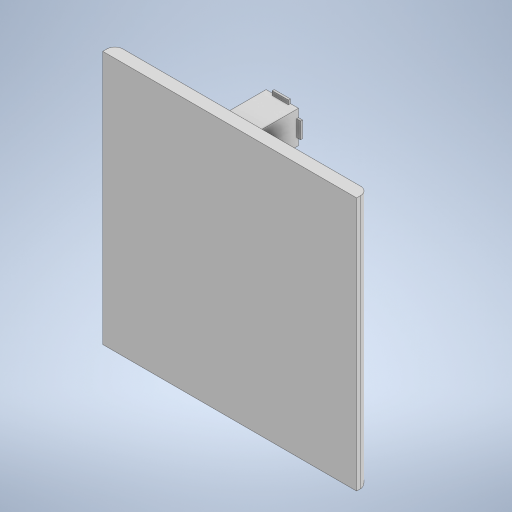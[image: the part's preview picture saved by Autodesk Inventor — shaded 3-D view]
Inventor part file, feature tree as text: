
AUTODESK INVENTOR PART (.ipt)
format: ipt  version: 2024 (Build 280153000, 153)  size: 258,048 bytes
history: native  units: mm
features: extrude x3, sketch x3, fillet x1
ambient origin geometry x8: Origin, YZ Plane, XZ Plane, XY Plane, X Axis, Y Axis, Z Axis, Center Point
bodies: Volumenkörper1 (feature_tree)
feature tree (7):
  extrude  "Extrusion1"  Depth=62.7mm
  extrude  "Extrusion2"  Depth=1.0mm
  extrude  "Extrusion3"  Depth=4.0mm
  fillet  "Rundung1"  Radius=4.0mm
  sketch  "Skizze1"  dims[d0=62.7mm d1=62.7mm]
  sketch  "Skizze2"  dims[d2=3.0mm d3=0.0mm d6=1.0mm]
  sketch  "Skizze3"  dims[d7=8.0mm d9=4.0mm d10=4.0mm d11=10.0mm d12=0.0mm d16=0.5mm d17=0.0mm d18=1.0mm d19=1.0mm d21=1.0mm d22=1.0mm d23=2.0mm d24=2.0mm d25=2.0mm d26=2.0mm d27=2.0mm d28=2.0mm d29=2.0mm d30=2.0mm]
